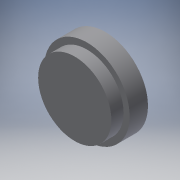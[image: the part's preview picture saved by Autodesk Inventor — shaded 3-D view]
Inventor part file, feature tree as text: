
AUTODESK INVENTOR PART (.ipt)
format: ipt  version: 2019 (Build 230136000, 136)  size: 121,856 bytes
history: native  units: mm
features: extrude x3, sketch x2, fillet x1
ambient origin geometry x8: Origin, YZ Plane, XZ Plane, XY Plane, X Axis, Y Axis, Z Axis, Center Point
bodies: Solid1 (feature_tree)
feature tree (6):
  sketch  "Sketch1"  dims[d0=12.0mm d1=14.0mm]
  extrude  "Extrusion1"  Depth=14.0mm
  extrude  "Extrusion2"  Depth=3.0mm TaperAngle=0.0deg
  extrude  "Extrusion3"  Depth=10.0mm
  fillet  "Fillet1"  Radius=1.0mm
  sketch  "Sketch2"  dims[d2=4.0mm d3=0.0mm d4=3.0mm d5=0.0mm d6=10.0mm d7=1.0mm d8=0.0mm d9=5.0mm]
